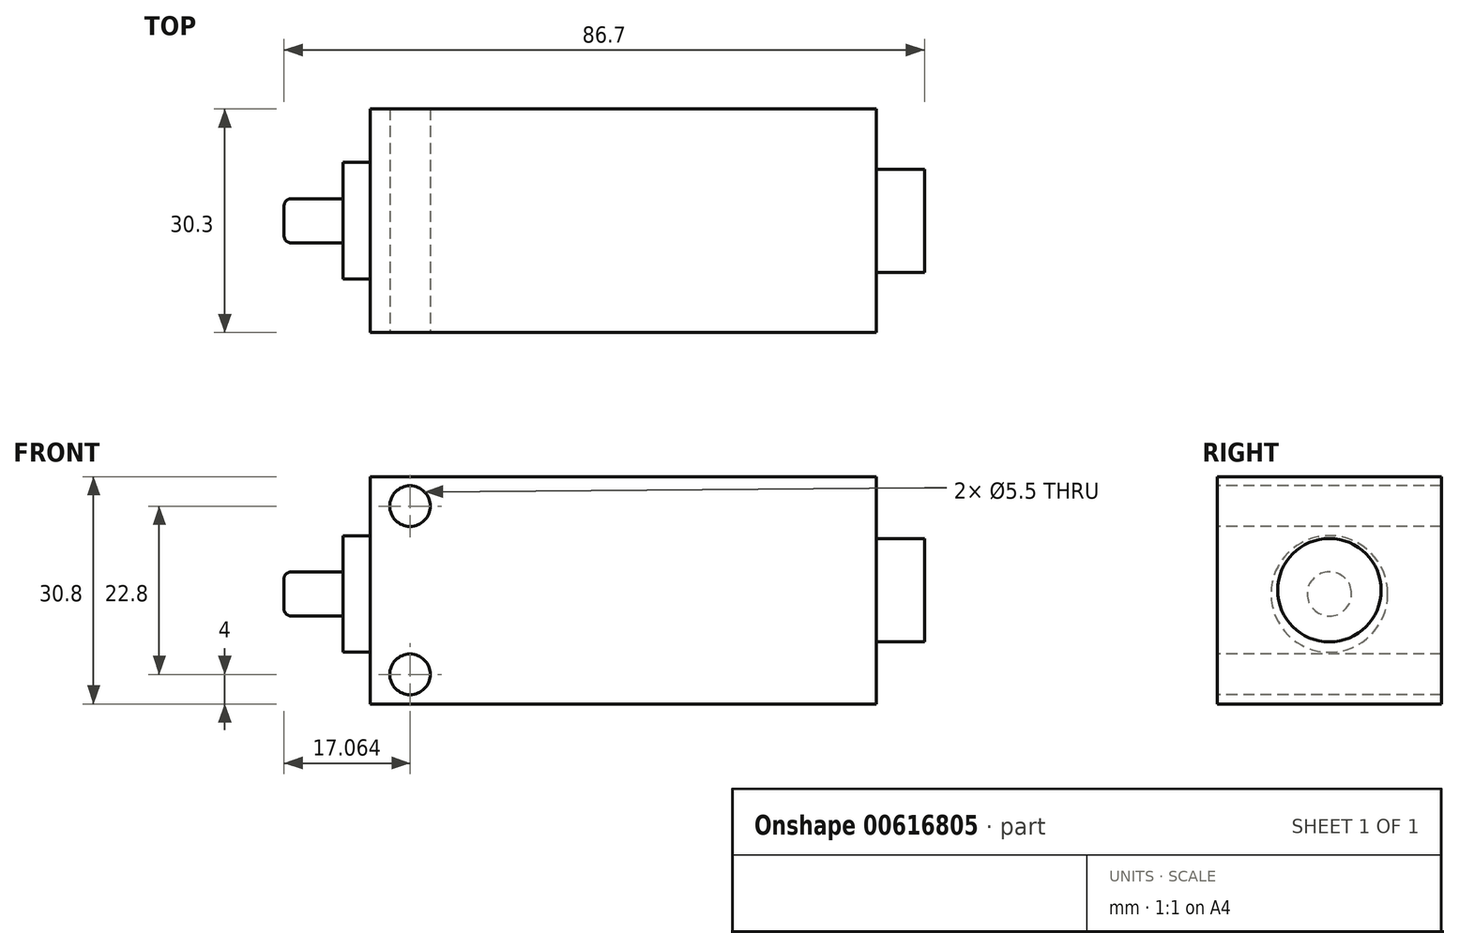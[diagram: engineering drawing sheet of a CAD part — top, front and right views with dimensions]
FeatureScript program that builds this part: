
annotation { "Feature Type Name" : "Feature", "Feature Type Description" : "" }
export const myFeature = defineFeature(function(context is Context, id is Id, definition is map)
    precondition{}
    {
        {
            var Q0;
            Q0=qCreatedBy(makeId("Top.planeOp"),FACE);
            var sketch = newSketch(context, id + "F0", { "sketchPlane" : qUnion([Q0])});
            skLineSegment(sketch, "E0.bottom", {"start": v(34.25, 15.15) * mm, "end": v(-34.25, 15.15) * mm});
            skLineSegment(sketch, "E0.top", {"start": v(34.25, -15.15) * mm, "end": v(-34.25, -15.15) * mm});
            skLineSegment(sketch, "E0.left", {"start": v(34.25, 15.15) * mm, "end": v(34.25, -15.15) * mm});
            skLineSegment(sketch, "E0.right", {"start": v(-34.25, 15.15) * mm, "end": v(-34.25, -15.15) * mm});
            skPoint(sketch, "E0.middle", {"position": v(0, 0) * mm});
            skSolve(sketch);
        }
        {
            var Q0;
            Q0=qSketchRegion(id+"F0",true);
            extrude(context, id + "F1", {"entities" : qUnion([Q0]), "depth" : 30.8 * mm, "offsetDistance" : 25 * mm});
        }
        {
            var Q0;
            Q0=makeQuery(id+"F1.opExtrude","SWEPT_FACE",FACE,{"disambiguationData":[OSD([sQuery(id+"F0.wireOp",EDGE,"E0.right")])]});
            var sketch = newSketch(context, id + "F2", { "sketchPlane" : qUnion([Q0])});
            skPoint(sketch, "E1.middle", {"position": v(0, 7.45) * mm});
            skCircle(sketch, "E2.converted", {"center": v(0, 14.9) * mm, "radius": 7.9 * mm});
            skSolve(sketch);
        }
        {
            var Q0;
            Q0=qSketchRegion(id+"F2",true);
            extrude(context, id + "F3", {"entities" : qUnion([Q0]), "operationType" : NewBodyOperationType.ADD, "depth" : 3.7 * mm, "offsetDistance" : 25 * mm});
        }
        {
            var Q0;
            Q0=makeQuery(id+"F1.opExtrude","SWEPT_FACE",FACE,{"disambiguationData":[OSD([sQuery(id+"F0.wireOp",EDGE,"E0.left")])]});
            var sketch = newSketch(context, id + "F4", { "sketchPlane" : qUnion([Q0])});
            skCircle(sketch, "E3", {"center": v(0, 15.4) * mm, "radius": 7 * mm});
            skLineSegment(sketch, "E4", {"start": v(-15.15, 15.4) * mm, "end": v(15.15, 15.4) * mm, "construction": true});
            skLineSegment(sketch, "E5", {"start": v(0, 30.8) * mm, "end": v(0, 0) * mm, "construction": true});
            skSolve(sketch);
        }
        {
            var Q0;
            Q0=qSketchRegion(id+"F4",true);
            extrude(context, id + "F5", {"entities" : qUnion([Q0]), "operationType" : NewBodyOperationType.ADD, "depth" : 6.5 * mm, "offsetDistance" : 25 * mm});
        }
        {
            var Q0;
            Q0=makeQuery(id+"F1.opExtrude","SWEPT_FACE",FACE,{"disambiguationData":[OSD([sQuery(id+"F0.wireOp",EDGE,"E0.bottom")])]});
            var sketch = newSketch(context, id + "F6", { "sketchPlane" : qUnion([Q0])});
            skPoint(sketch, "E6", {"position": v(28.89, 26.8) * mm});
            skLineSegment(sketch, "E7", {"start": v(65.89, 0) * mm, "end": v(65.89, 34.5) * mm, "construction": true});
            skPoint(sketch, "E8", {"position": v(28.89, 4) * mm});
            skSolve(sketch);
        }
        {
            var Q0;
            Q0=sQuery(id+"F6.wireOp",VERTEX,"E6");
            var Q1;
            Q1=sQuery(id+"F6.wireOp",VERTEX,"E8");
            var Q2;
            Q2=makeQuery(id+"F1.opExtrude","SWEPT_BODY",BODY,{"disambiguationData":[OSD([sQuery(id+"F0.wireOp",EDGE,"E0.bottom"),sQuery(id+"F0.wireOp",EDGE,"E0.top"),sQuery(id+"F0.wireOp",EDGE,"E0.left"),sQuery(id+"F0.wireOp",EDGE,"E0.right")])]});
            hole(context, id + "F7", {"style" : HoleStyle.SIMPLE, "endStyle" : HoleEndStyle.THROUGH, "standardTappedOrClearance" : lookupTablePath({ "fit" : "Normal", "standard" : "ISO", "size" : "M5", "type" : "Clearance" }), "standardBlindInLast" : lookupTablePath({ "fit" : "Standard", "standard" : "ISO", "size" : "M5", "type" : "Clearance" }), "holeDiameter" : 5.5 * mm, "majorDiameter" : 5 * mm, "isTappedThrough" : true, "tappedDepth" : 3.9 * mm, "tapClearance" : 3, "locations" : qUnion([Q0, Q1]), "scope" : qUnion([Q2]), "startStyle" : HoleStartStyle.PART});
        }
        {
            var Q0;
            Q0=makeQuery(id+"F3.opExtrude","CAP_FACE",FACE,{"disambiguationData":[OSD([sQuery(id+"F2.wireOp",EDGE,"E2.converted")])],"isStart":false});
            var sketch = newSketch(context, id + "F8", { "sketchPlane" : qUnion([Q0])});
            skCircle(sketch, "E9", {"center": v(0, 14.9) * mm, "radius": 3 * mm});
            skSolve(sketch);
        }
        {
            var Q0;
            Q0=makeQuery(id+"F8.imprint","IMPRINT",FACE,{"disambiguationData":[TD([[makeQuery(id+"F8.imprint","IMPRINT",EDGE,{"derivedFrom":sQuery(id+"F8.wireOp",EDGE,"E9")}),1.0]])]});
            extrude(context, id + "F9", {"entities" : qUnion([Q0]), "operationType" : NewBodyOperationType.ADD, "depth" : 8 * mm, "offsetDistance" : 25 * mm});
        }
        {
            var Q0;
            Q0=makeQuery(id+"F9.opExtrude","CAP_EDGE",EDGE,{"disambiguationData":[OSD([sQuery(id+"F8.wireOp",EDGE,"E9")])],"isStart":false});
            fillet(context, id + "F10", {"entities" : qUnion([Q0]), "radius" : 1 * mm, "tangentPropagation" : true, "allowEdgeOverflow" : false});
        }
    });
